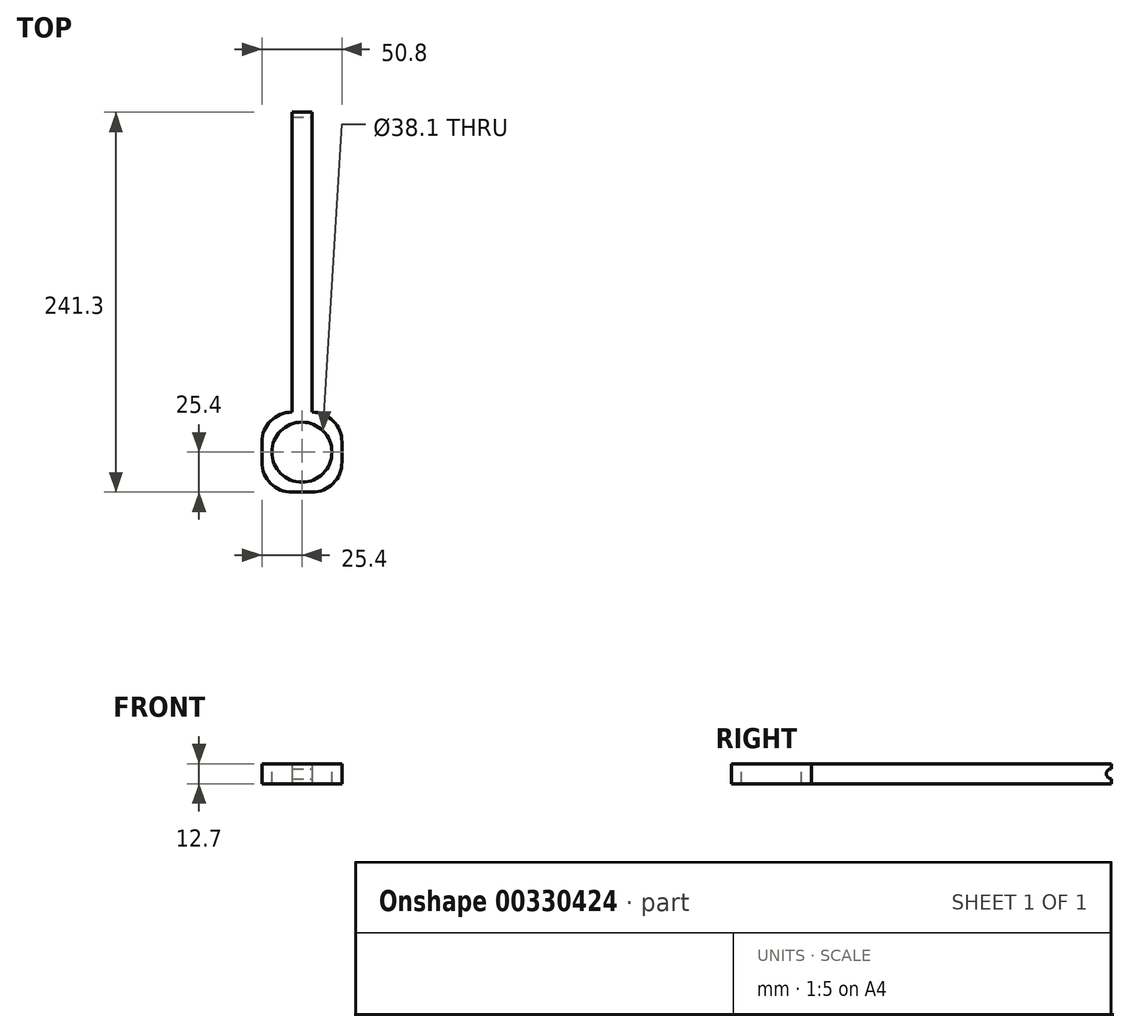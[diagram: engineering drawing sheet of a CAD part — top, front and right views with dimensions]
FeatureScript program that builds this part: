
annotation { "Feature Type Name" : "Feature", "Feature Type Description" : "" }
export const myFeature = defineFeature(function(context is Context, id is Id, definition is map)
    precondition{}
    {
        {
            var Q0;
            Q0=qCreatedBy(makeId("Front.planeOp"),FACE);
            var sketch = newSketch(context, id + "F0", { "sketchPlane" : qUnion([Q0])});
            skLineSegment(sketch, "E0.bottom", {"start": v(0, 0) * mm, "end": v(12.7, 0) * mm});
            skLineSegment(sketch, "E0.top", {"start": v(0, -12.7) * mm, "end": v(12.7, -12.7) * mm});
            skLineSegment(sketch, "E0.left", {"start": v(0, 0) * mm, "end": v(0, -12.7) * mm});
            skLineSegment(sketch, "E0.right", {"start": v(12.7, 0) * mm, "end": v(12.7, -12.7) * mm});
            skSolve(sketch);
        }
        {
            var Q0;
            Q0 = qSketchRegion(id + "F0", true);
            extrude(context, id + "F1", {"entities" : qUnion([Q0]), "depth" : 190.5 * mm});
        }
        {
            var Q0;
            Q0=makeQuery(id+"F1.opExtrude","SWEPT_FACE",FACE,{"disambiguationData":[OSD([sQuery(id+"F0.wireOp",EDGE,"E0.bottom")])]});
            var sketch = newSketch(context, id + "F2", { "sketchPlane" : qUnion([Q0])});
            skLineSegment(sketch, "E1.bottom", {"start": v(31.75, -190.5) * mm, "end": v(-19.05, -190.5) * mm});
            skLineSegment(sketch, "E1.top", {"start": v(31.75, -241.3) * mm, "end": v(-19.05, -241.3) * mm});
            skLineSegment(sketch, "E1.left", {"start": v(31.75, -190.5) * mm, "end": v(31.75, -241.3) * mm});
            skLineSegment(sketch, "E1.right", {"start": v(-19.05, -190.5) * mm, "end": v(-19.05, -241.3) * mm});
            skSolve(sketch);
        }
        {
            var Q0;
            Q0 = qSketchRegion(id + "F2", true);
            extrude(context, id + "F3", {"entities" : qUnion([Q0]), "operationType" : NewBodyOperationType.ADD, "oppositeDirection" : true, "depth" : 12.7 * mm});
        }
        {
            var Q0;
            Q0=makeQuery(id+"F3.boolean.opBoolean","MERGE",FACE,{"derivedFrom":[makeQuery(id+"F1.opExtrude","SWEPT_FACE",FACE,{"disambiguationData":[OSD([sQuery(id+"F0.wireOp",EDGE,"E0.bottom")])]}),makeQuery(id+"F3.opExtrude","CAP_FACE",FACE,{"disambiguationData":[OSD([sQuery(id+"F2.wireOp",EDGE,"E1.bottom"),sQuery(id+"F2.wireOp",EDGE,"E1.top"),sQuery(id+"F2.wireOp",EDGE,"E1.left"),sQuery(id+"F2.wireOp",EDGE,"E1.right")])],"isStart":true})]});
            var sketch = newSketch(context, id + "F4", { "sketchPlane" : qUnion([Q0])});
            skCircle(sketch, "E2", {"center": v(6.35, -215.9) * mm, "radius": 19.05 * mm});
            skPoint(sketch, "E2.centerSnap0", {"position": v(-19.05, -215.9) * mm});
            skPoint(sketch, "E2.centerSnap1", {"position": v(6.35, -241.3) * mm});
            skSolve(sketch);
        }
        {
            var Q0;
            Q0 = qSketchRegion(id + "F4", true);
            extrude(context, id + "F5", {"entities" : qUnion([Q0]), "operationType" : NewBodyOperationType.REMOVE, "endBound" : BoundingType.THROUGH_ALL, "oppositeDirection" : true, "depth" : 25.4 * mm});
        }
        {
            var Q0;
            Q0=makeQuery(id+"F3.opExtrude","SWEPT_EDGE",EDGE,{"disambiguationData":[OSD([sQuery(id+"F2.wireOp",EDGE,"E1.top"),sQuery(id+"F2.wireOp",EDGE,"E1.left")])]});
            var Q1;
            Q1=makeQuery(id+"F3.opExtrude","SWEPT_EDGE",EDGE,{"disambiguationData":[OSD([sQuery(id+"F2.wireOp",EDGE,"E1.bottom"),sQuery(id+"F2.wireOp",EDGE,"E1.left")])]});
            var Q2;
            Q2=makeQuery(id+"F3.opExtrude","SWEPT_EDGE",EDGE,{"disambiguationData":[OSD([sQuery(id+"F2.wireOp",EDGE,"E1.top"),sQuery(id+"F2.wireOp",EDGE,"E1.right")])]});
            var Q3;
            Q3=makeQuery(id+"F3.opExtrude","SWEPT_EDGE",EDGE,{"disambiguationData":[OSD([sQuery(id+"F2.wireOp",EDGE,"E1.bottom"),sQuery(id+"F2.wireOp",EDGE,"E1.right")])]});
            fillet(context, id + "F6", {"entities" : qUnion([Q0, Q1, Q2, Q3]), "radius" : 19.05 * mm, "tangentPropagation" : true, "allowEdgeOverflow" : false});
        }
        {
            var Q0;
            Q0=makeQuery(id+"F1.opExtrude","SWEPT_FACE",FACE,{"disambiguationData":[OSD([sQuery(id+"F0.wireOp",EDGE,"E0.right")])]});
            var sketch = newSketch(context, id + "F7", { "sketchPlane" : qUnion([Q0])});
            skCircle(sketch, "E3", {"center": v(0, -6.35) * mm, "radius": 3.18 * mm});
            skSolve(sketch);
        }
        {
            var Q0;
            Q0 = qSketchRegion(id + "F7", true);
            extrude(context, id + "F8", {"entities" : qUnion([Q0]), "operationType" : NewBodyOperationType.REMOVE, "endBound" : BoundingType.THROUGH_ALL, "oppositeDirection" : true, "depth" : 25.4 * mm});
        }
    });
